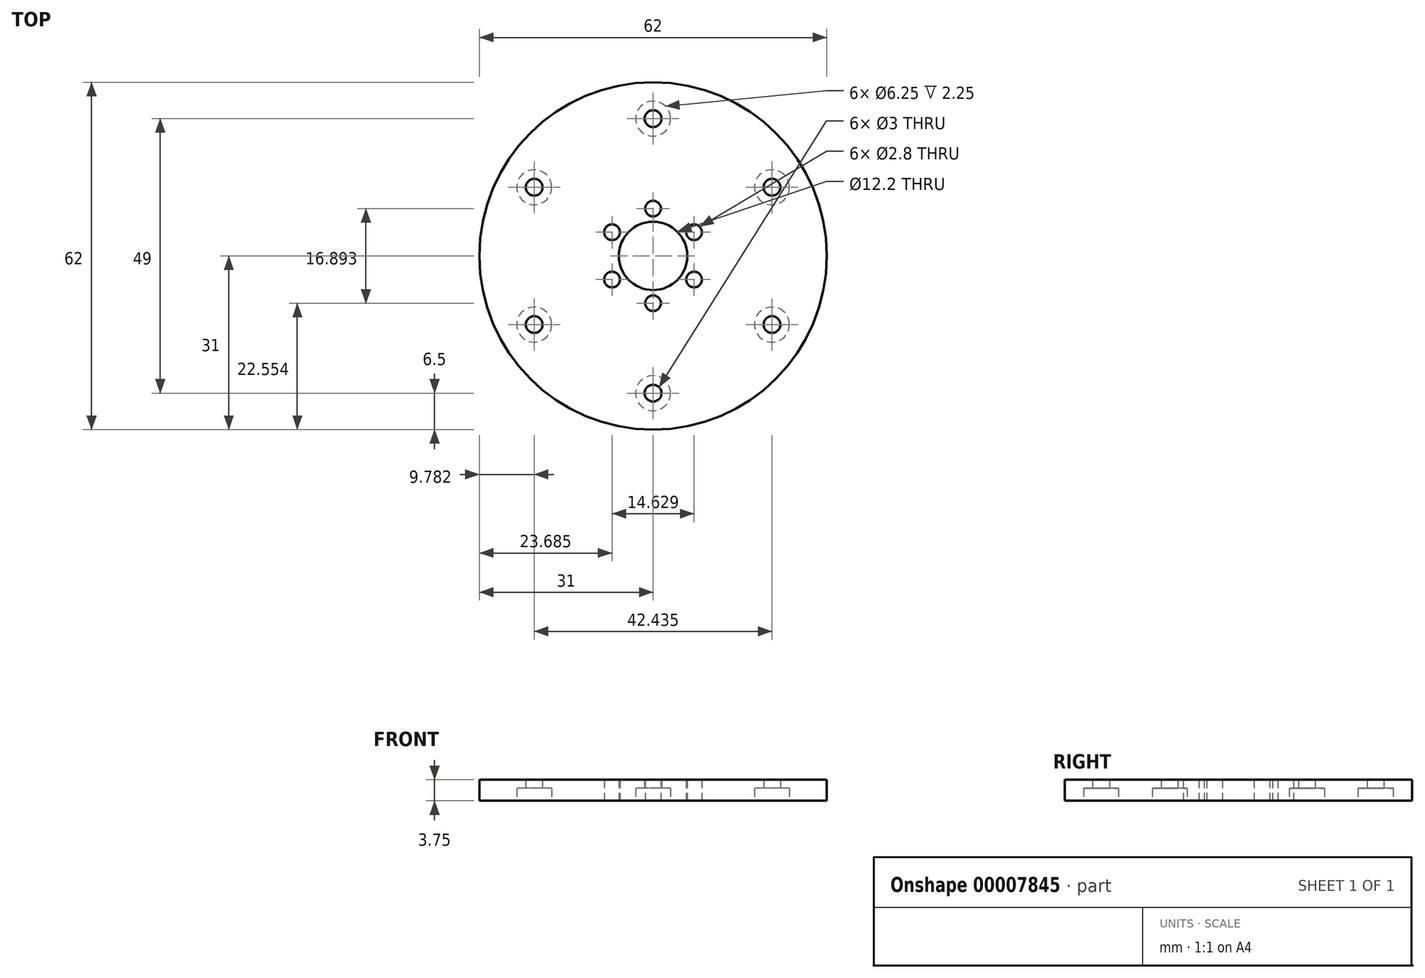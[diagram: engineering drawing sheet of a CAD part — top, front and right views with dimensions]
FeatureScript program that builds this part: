
annotation { "Feature Type Name" : "Feature", "Feature Type Description" : "" }
export const myFeature = defineFeature(function(context is Context, id is Id, definition is map)
    precondition{}
    {
        {
            var Q0;
            Q0=qCreatedBy(makeId("Top.planeOp"),FACE);
            var sketch = newSketch(context, id + "F0", { "sketchPlane" : qUnion([Q0])});
            skCircle(sketch, "E0", {"center": v(0, 0) * mm, "radius": 31 * mm});
            skCircle(sketch, "E1", {"center": v(0, 0) * mm, "radius": 6.1 * mm});
            skSolve(sketch);
        }
        {
            var Q0;
            Q0=qCreatedBy(makeId("Top.planeOp"),FACE);
            var sketch = newSketch(context, id + "F1", { "sketchPlane" : qUnion([Q0])});
            skCircle(sketch, "E2", {"center": v(0, -24.5) * mm, "radius": 3.12 * mm});
            skCircle(sketch, "E3.1.0", {"center": v(21.22, -12.25) * mm, "radius": 3.12 * mm});
            skCircle(sketch, "E3.2.0", {"center": v(21.22, 12.25) * mm, "radius": 3.12 * mm});
            skCircle(sketch, "E3.3.0", {"center": v(0, 24.5) * mm, "radius": 3.12 * mm});
            skCircle(sketch, "E3.4.0", {"center": v(-21.22, 12.25) * mm, "radius": 3.12 * mm});
            skCircle(sketch, "E3.5.0", {"center": v(-21.22, -12.25) * mm, "radius": 3.12 * mm});
            skPoint(sketch, "E3.center", {"position": v(0, 0) * mm});
            skSolve(sketch);
        }
        {
            var Q0;
            Q0=makeQuery(id+"F0.imprint","IMPRINT",FACE,{"disambiguationData":[TD([[makeQuery(id+"F0.imprint","IMPRINT",EDGE,{"derivedFrom":sQuery(id+"F0.wireOp",EDGE,"E0")}),1.0]])]});
            var Q1;
            Q1=sQuery(id+"F0.wireOp",EDGE,"E0");
            extrude(context, id + "F2", {"entities" : qUnion([Q0]), "surfaceEntities" : qUnion([Q1]), "depth" : 3.75 * mm});
        }
        {
            var Q0;
            Q0=qSketchRegion(id+"F1",true);
            extrude(context, id + "F3", {"entities" : qUnion([Q0]), "operationType" : NewBodyOperationType.REMOVE, "depth" : 2.25 * mm});
        }
        {
            var Q0;
            Q0=qCreatedBy(makeId("Top.planeOp"),FACE);
            var sketch = newSketch(context, id + "F4", { "sketchPlane" : qUnion([Q0])});
            skCircle(sketch, "E4", {"center": v(0, 24.5) * mm, "radius": 1.5 * mm});
            skCircle(sketch, "E5.1.0", {"center": v(-21.22, 12.25) * mm, "radius": 1.5 * mm});
            skCircle(sketch, "E5.2.0", {"center": v(-21.22, -12.25) * mm, "radius": 1.5 * mm});
            skCircle(sketch, "E5.3.0", {"center": v(0, -24.5) * mm, "radius": 1.5 * mm});
            skCircle(sketch, "E5.4.0", {"center": v(21.22, -12.25) * mm, "radius": 1.5 * mm});
            skCircle(sketch, "E5.5.0", {"center": v(21.22, 12.25) * mm, "radius": 1.5 * mm});
            skPoint(sketch, "E5.center", {"position": v(0, 0) * mm});
            skSolve(sketch);
        }
        {
            var Q0;
            Q0=qSketchRegion(id+"F4",true);
            var Q1;
            Q1=sQuery(id+"F4.wireOp",EDGE,"E4");
            var Q2;
            Q2=sQuery(id+"F4.wireOp",EDGE,"E5.5.0");
            var Q3;
            Q3=sQuery(id+"F4.wireOp",EDGE,"E5.4.0");
            var Q4;
            Q4=sQuery(id+"F4.wireOp",EDGE,"E5.3.0");
            var Q5;
            Q5=sQuery(id+"F4.wireOp",EDGE,"E5.2.0");
            var Q6;
            Q6=sQuery(id+"F4.wireOp",EDGE,"E5.1.0");
            extrude(context, id + "F5", {"entities" : qUnion([Q0]), "operationType" : NewBodyOperationType.REMOVE, "surfaceEntities" : qUnion([Q1, Q2, Q3, Q4, Q5, Q6]), "depth" : 100 * mm});
        }
        {
            var Q0;
            Q0=qCreatedBy(makeId("Top.planeOp"),FACE);
            var sketch = newSketch(context, id + "F6", { "sketchPlane" : qUnion([Q0])});
            skCircle(sketch, "E6.1.0", {"center": v(0, 8.45) * mm, "radius": 1.4 * mm});
            skPoint(sketch, "E6.center", {"position": v(0, 0) * mm});
            skCircle(sketch, "E7.1.0", {"center": v(-7.31, 4.22) * mm, "radius": 1.4 * mm});
            skCircle(sketch, "E7.2.0", {"center": v(-7.31, -4.22) * mm, "radius": 1.4 * mm});
            skCircle(sketch, "E7.3.0", {"center": v(0, -8.45) * mm, "radius": 1.4 * mm});
            skCircle(sketch, "E7.4.0", {"center": v(7.31, -4.22) * mm, "radius": 1.4 * mm});
            skCircle(sketch, "E7.5.0", {"center": v(7.31, 4.22) * mm, "radius": 1.4 * mm});
            skSolve(sketch);
        }
        {
            var Q0;
            Q0=qSketchRegion(id+"F6",true);
            var Q1;
            Q1=sQuery(id+"F6.wireOp",EDGE,"19aad8b8-8518-4f5a-bb88-8280c607c455");
            extrude(context, id + "F7", {"entities" : qUnion([Q0]), "operationType" : NewBodyOperationType.REMOVE, "surfaceEntities" : qUnion([Q1]), "endBound" : BoundingType.THROUGH_ALL, "depth" : 25 * mm});
        }
    });
